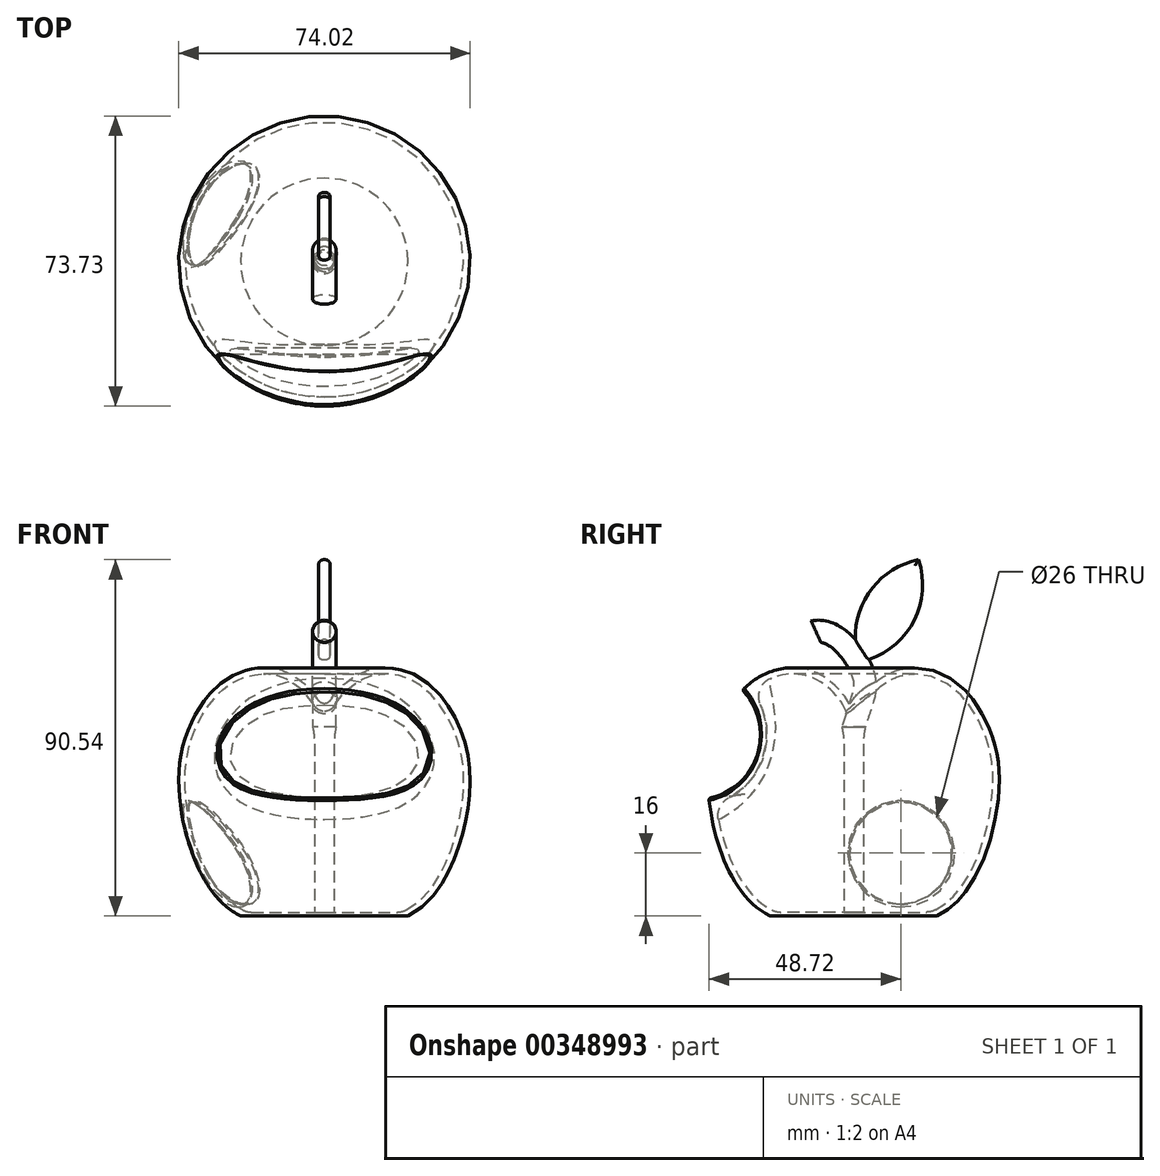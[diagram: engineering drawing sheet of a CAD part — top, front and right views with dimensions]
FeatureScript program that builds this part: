
annotation { "Feature Type Name" : "Feature", "Feature Type Description" : "" }
export const myFeature = defineFeature(function(context is Context, id is Id, definition is map)
    precondition{}
    {
        {
            var Q0;
            Q0=qCreatedBy(makeId("Right.planeOp"),FACE);
            var sketch = newSketch(context, id + "F0", { "sketchPlane" : qUnion([Q0])});
            skLineSegment(sketch, "E0", {"start": v(0, 37.78) * mm, "end": v(0, -10) * mm});
            skFitSpline(sketch, "E1", {"points": [v(0, 37.78) * mm, v(-1.44, 40.7) * mm, v(-10.29, 50.45) * mm, v(-23.9, 48.93) * mm, v(-32.64, 37.78) * mm, v(-35.4, 25.8) * mm, v(-33.05, 9.45) * mm, v(-25.91, -4.4) * mm, v(-15.84, -10.1) * mm, v(0, -10) * mm], "startDerivative": vector(-75.89, 4.24) * mm, "endDerivative": vector(137.22, 0) * mm});
            skSolve(sketch);
        }
        {
            var Q0;
            Q0=makeQuery(id+"F0.imprint","IMPRINT",FACE,{"disambiguationData":[TD([[makeQuery(id+"F0.imprint","IMPRINT",EDGE,{"derivedFrom":sQuery(id+"F0.wireOp",EDGE,"E0")}),-1.0]])]});
            var Q1;
            Q1=sQuery(id+"F0.wireOp",EDGE,"E0");
            revolve(context, id + "F1", {"entities" : qUnion([Q0]), "axis" : qUnion([Q1]), "revolveType" : RevolveType.FULL});
        }
        {
            var Q0;
            Q0=qCreatedBy(makeId("Top.planeOp"),FACE);
            cPlane(context, id + "F2", {"entities" : qUnion([Q0]), "cplaneType" : CPlaneType.OFFSET, "offset" : 38.1 * mm, "width" : 152.4 * mm, "height" : 152.4 * mm});
        }
        {
            var Q0;
            Q0=qCreatedBy(makeId("Right.planeOp"),FACE);
            var sketch = newSketch(context, id + "F3", { "sketchPlane" : qUnion([Q0])});
            skCircle(sketch, "E2", {"center": v(-40, 36) * mm, "radius": 18 * mm});
            skSolve(sketch);
        }
        {
            var Q0;
            Q0 = qSketchRegion(id + "F3", true);
            extrude(context, id + "F4", {"entities" : qUnion([Q0]), "operationType" : NewBodyOperationType.REMOVE, "depth" : 50.8 * mm, "hasSecondDirection" : true, "secondDirectionOppositeDirection" : true, "secondDirectionDepth" : 50.8 * mm});
        }
        {
            var Q0;
            Q0=qCreatedBy(makeId("Right.planeOp"),FACE);
            var sketch = newSketch(context, id + "F5", { "sketchPlane" : qUnion([Q0])});
            skLineSegment(sketch, "E3.bottom", {"start": v(25, -10) * mm, "end": v(-25, -10) * mm});
            skLineSegment(sketch, "E3.top", {"start": v(25, -20) * mm, "end": v(-25, -20) * mm});
            skLineSegment(sketch, "E3.left", {"start": v(25, -10) * mm, "end": v(25, -20) * mm});
            skLineSegment(sketch, "E3.right", {"start": v(-25, -10) * mm, "end": v(-25, -20) * mm});
            skSolve(sketch);
        }
        {
            var Q0;
            Q0 = qSketchRegion(id + "F5", true);
            extrude(context, id + "F6", {"entities" : qUnion([Q0]), "operationType" : NewBodyOperationType.REMOVE, "oppositeDirection" : true, "depth" : 25 * mm, "hasSecondDirection" : true, "secondDirectionOppositeDirection" : false, "secondDirectionDepth" : 25 * mm});
        }
        {
            var Q0;
            Q0=makeQuery(id+"F6.boolean.opBoolean","COPY",FACE,{"derivedFrom":makeQuery(id+"F6.opExtrude","SWEPT_FACE",FACE,{"disambiguationData":[OSD([sQuery(id+"F5.wireOp",EDGE,"E3.bottom")])]})});
            shell(context, id + "F7", {"entities" : qUnion([Q0]), "thickness" : 1.6 * mm, "oppositeDirection" : true});
        }
        {
            var Q0;
            Q0=qCreatedBy(makeId("Right.planeOp"),FACE);
            var sketch = newSketch(context, id + "F8", { "sketchPlane" : qUnion([Q0])});
            skFitSpline(sketch, "E4", {"points": [v(0, 38.1) * mm, v(2.11, 52.38) * mm, v(-9.55, 62.26) * mm], "startDerivative": vector(16.25, 49.37) * mm, "endDerivative": vector(-31.32, -3.4) * mm});
            skSolve(sketch);
        }
        {
            var Q0;
            Q0=qCreatedBy(id+"F2.planeOp",FACE);
            var sketch = newSketch(context, id + "F9", { "sketchPlane" : qUnion([Q0])});
            skCircle(sketch, "E5", {"center": v(0, 0) * mm, "radius": 2.98 * mm});
            skSolve(sketch);
        }
        {
            var Q0;
            Q0=makeQuery(id+"F9.imprint","IMPRINT",FACE,{"disambiguationData":[TD([[makeQuery(id+"F9.imprint","IMPRINT",EDGE,{"derivedFrom":sQuery(id+"F9.wireOp",EDGE,"E5")}),1.0]])]});
            var Q1;
            Q1=sQuery(id+"F8.wireOp",EDGE,"E4");
            sweep(context, id + "F10", {"operationType" : NewBodyOperationType.ADD, "profiles" : qUnion([Q0]), "path" : qUnion([Q1])});
        }
        {
            var Q0;
            Q0=qCreatedBy(makeId("Right.planeOp"),FACE);
            var sketch = newSketch(context, id + "F11", { "sketchPlane" : qUnion([Q0])});
            skCircle(sketch, "E6", {"center": v(12, 6) * mm, "radius": 13 * mm});
            skSolve(sketch);
        }
        {
            var Q0;
            Q0 = qSketchRegion(id + "F11", true);
            extrude(context, id + "F12", {"entities" : qUnion([Q0]), "operationType" : NewBodyOperationType.REMOVE, "oppositeDirection" : true, "depth" : 55 * mm});
        }
        {
            var Q0;
            Q0=makeQuery(id+"F6.boolean.opBoolean","COPY",FACE,{"derivedFrom":makeQuery(id+"F6.opExtrude","SWEPT_FACE",FACE,{"disambiguationData":[OSD([sQuery(id+"F5.wireOp",EDGE,"E3.bottom")])]})});
            var sketch = newSketch(context, id + "F13", { "sketchPlane" : qUnion([Q0])});
            skCircle(sketch, "E7.0", {"center": v(0, 0) * mm, "radius": 21.23 * mm});
            skSolve(sketch);
        }
        {
            var Q0;
            Q0 = qSketchRegion(id + "F13", true);
            extrude(context, id + "F14", {"entities" : qUnion([Q0]), "operationType" : NewBodyOperationType.ADD, "oppositeDirection" : true, "depth" : 1 * mm});
        }
        {
            var Q0;
            Q0=makeQuery(id+"F14.opExtrude","CAP_FACE",FACE,{"disambiguationData":[OSD([sQuery(id+"F13.wireOp",EDGE,"E7.0")])],"isStart":false});
            var sketch = newSketch(context, id + "F15", { "sketchPlane" : qUnion([Q0])});
            skCircle(sketch, "E8", {"center": v(0, 0) * mm, "radius": 2.5 * mm});
            skSolve(sketch);
        }
        {
            var Q0;
            Q0 = qSketchRegion(id + "F15", true);
            extrude(context, id + "F16", {"entities" : qUnion([Q0]), "operationType" : NewBodyOperationType.ADD, "depth" : 48 * mm});
        }
        {
            var Q0;
            Q0=makeQuery(id+"F16.boolean.opBoolean","INTERSECT",EDGE,{"derivedFrom":[makeQuery(id+"F10.opSweep","CAP_FACE",FACE,{"disambiguationData":[OSD([sQuery(id+"F8.wireOp",VERTEX,"E4.start"),sQuery(id+"F9.wireOp",EDGE,"E5")])],"isStart":true}),makeQuery(id+"F16.opExtrude","SWEPT_FACE",FACE,{"disambiguationData":[OSD([sQuery(id+"F15.wireOp",EDGE,"E8")])]})]});
            fillet(context, id + "F17", {"entities" : qUnion([Q0]), "radius" : 20 * mm, "tangentPropagation" : true, "allowEdgeOverflow" : false});
        }
        {
            var Q0;
            Q0=makeQuery(id+"F16.opExtrude","CAP_EDGE",EDGE,{"disambiguationData":[OSD([sQuery(id+"F15.wireOp",EDGE,"E8")])],"isStart":true});
            var Q1;
            Q1=makeQuery(id+"F14.boolean.opBoolean","INTERSECT",EDGE,{"derivedFrom":[makeQuery(id+"F10.boolean.opBoolean","SPLIT",FACE,{"disambiguationData":[TD([makeQuery(id+"F6.boolean.opBoolean","COPY",FACE,{"derivedFrom":makeQuery(id+"F6.opExtrude","SWEPT_FACE",FACE,{"disambiguationData":[OSD([sQuery(id+"F5.wireOp",EDGE,"E3.bottom")])]})})])],"derivedFrom":makeQuery(id+"F7.opShell","OFFSET_FACE",FACE,{"disambiguationData":[OSD([sQuery(id+"F0.wireOp",EDGE,"E1")]),OD(1.0)]})}),makeQuery(id+"F14.opExtrude","CAP_FACE",FACE,{"disambiguationData":[OSD([sQuery(id+"F13.wireOp",EDGE,"E7.0")])],"isStart":false})]});
            fillet(context, id + "F18", {"entities" : qUnion([Q0, Q1]), "radius" : 5 * mm, "tangentPropagation" : true, "allowEdgeOverflow" : false});
        }
        {
            var Q0;
            Q0=makeQuery(id+"F10.boolean.opBoolean","INTERSECT",EDGE,{"derivedFrom":[makeQuery(id+"F7.opShell","OFFSET_FACE",FACE,{"disambiguationData":[OSD([sQuery(id+"F0.wireOp",EDGE,"E1")]),OD(0.0)]}),makeQuery(id+"F10.opSweep","SWEPT_FACE",FACE,{"disambiguationData":[OSD([sQuery(id+"F8.wireOp",EDGE,"E4"),sQuery(id+"F9.wireOp",EDGE,"E5")])]})]});
            fillet(context, id + "F19", {"entities" : qUnion([Q0]), "radius" : 1 * mm, "tangentPropagation" : true, "allowEdgeOverflow" : false});
        }
        {
            var Q0;
            Q0=qCreatedBy(makeId("Right.planeOp"),FACE);
            var sketch = newSketch(context, id + "F20", { "sketchPlane" : qUnion([Q0])});
            skLineSegment(sketch, "E9", {"start": v(-30.84, -1.46) * mm, "end": v(31.2, 106) * mm, "construction": true});
            skPoint(sketch, "E10", {"position": v(-30, 0) * mm});
            skLineSegment(sketch, "E11", {"start": v(3.3, 70.84) * mm, "end": v(15.27, 63.93) * mm, "construction": true});
            skArc(sketch, "E12", {"start": v(1.5, 54.56) * mm, "mid": v(14.86, 64.16) * mm, "end": v(16.5, 80.54) * mm});
            skArc(sketch, "E13.MirrorCS", {"start": v(1.5, 54.56) * mm, "mid": v(3.14, 70.94) * mm, "end": v(16.5, 80.54) * mm});
            skSolve(sketch);
        }
        {
            var Q0;
            Q0 = qSketchRegion(id + "F20", true);
            extrude(context, id + "F21", {"entities" : qUnion([Q0]), "operationType" : NewBodyOperationType.ADD, "depth" : 1.5 * mm, "hasSecondDirection" : true, "secondDirectionOppositeDirection" : true, "secondDirectionDepth" : 1.5 * mm});
        }
        {
            var Q0;
            Q0=makeQuery(id+"F7.opShell","OFFSET_EDGE",EDGE,{"disambiguationData":[OSD([sQuery(id+"F0.wireOp",EDGE,"E1"),sQuery(id+"F3.wireOp",EDGE,"E2")])]});
            fillet(context, id + "F22", {"entities" : qUnion([Q0]), "radius" : 5 * mm, "tangentPropagation" : true, "allowEdgeOverflow" : false});
        }
        {
            var Q0;
            Q0=makeQuery(id+"F21.opExtrude","CAP_EDGE",EDGE,{"disambiguationData":[OSD([sQuery(id+"F20.wireOp",EDGE,"E13.MirrorCS")])],"isStart":true});
            var Q1;
            Q1=makeQuery(id+"F21.opExtrude","CAP_EDGE",EDGE,{"disambiguationData":[OSD([sQuery(id+"F20.wireOp",EDGE,"E13.MirrorCS")])],"isStart":false});
            var Q2;
            Q2=makeQuery(id+"F21.opExtrude","CAP_EDGE",EDGE,{"disambiguationData":[OSD([sQuery(id+"F20.wireOp",EDGE,"E12")])],"isStart":true});
            var Q3;
            Q3=makeQuery(id+"F21.opExtrude","CAP_EDGE",EDGE,{"disambiguationData":[OSD([sQuery(id+"F20.wireOp",EDGE,"E12")])],"isStart":false});
            fillet(context, id + "F23", {"entities" : qUnion([Q0, Q1, Q2, Q3]), "radius" : 1.2 * mm, "tangentPropagation" : true, "allowEdgeOverflow" : false});
        }
        {
            var Q0;
            Q0=makeQuery(id+"F12.boolean.opBoolean","INTERSECT",EDGE,{"derivedFrom":[makeQuery(id+"F1.opRevolve","SWEPT_FACE",FACE,{"disambiguationData":[OSD([sQuery(id+"F0.wireOp",EDGE,"E1")])]}),makeQuery(id+"F12.opExtrude","SWEPT_FACE",FACE,{"disambiguationData":[OSD([sQuery(id+"F11.wireOp",EDGE,"E6")])]})]});
            var Q1;
            Q1=makeQuery(id+"F12.boolean.opBoolean","INTERSECT",EDGE,{"derivedFrom":[makeQuery(id+"F10.boolean.opBoolean","SPLIT",FACE,{"disambiguationData":[TD([makeQuery(id+"F6.boolean.opBoolean","COPY",FACE,{"derivedFrom":makeQuery(id+"F6.opExtrude","SWEPT_FACE",FACE,{"disambiguationData":[OSD([sQuery(id+"F5.wireOp",EDGE,"E3.bottom")])]})})])],"derivedFrom":makeQuery(id+"F7.opShell","OFFSET_FACE",FACE,{"disambiguationData":[OSD([sQuery(id+"F0.wireOp",EDGE,"E1")])]})}),makeQuery(id+"F12.opExtrude","SWEPT_FACE",FACE,{"disambiguationData":[OSD([sQuery(id+"F11.wireOp",EDGE,"E6")])]})]});
            fillet(context, id + "F24", {"entities" : qUnion([Q0, Q1]), "radius" : 0.4 * mm, "tangentPropagation" : true, "allowEdgeOverflow" : false});
        }
        {
            var Q0;
            Q0=makeQuery(id+"F4.boolean.opBoolean","INTERSECT",EDGE,{"derivedFrom":[makeQuery(id+"F1.opRevolve","SWEPT_FACE",FACE,{"disambiguationData":[OSD([sQuery(id+"F0.wireOp",EDGE,"E1")])]}),makeQuery(id+"F4.opExtrude","SWEPT_FACE",FACE,{"disambiguationData":[OSD([sQuery(id+"F3.wireOp",EDGE,"E2")])]})]});
            fillet(context, id + "F25", {"entities" : qUnion([Q0]), "radius" : 0.6 * mm, "tangentPropagation" : true, "allowEdgeOverflow" : false});
        }
    });
